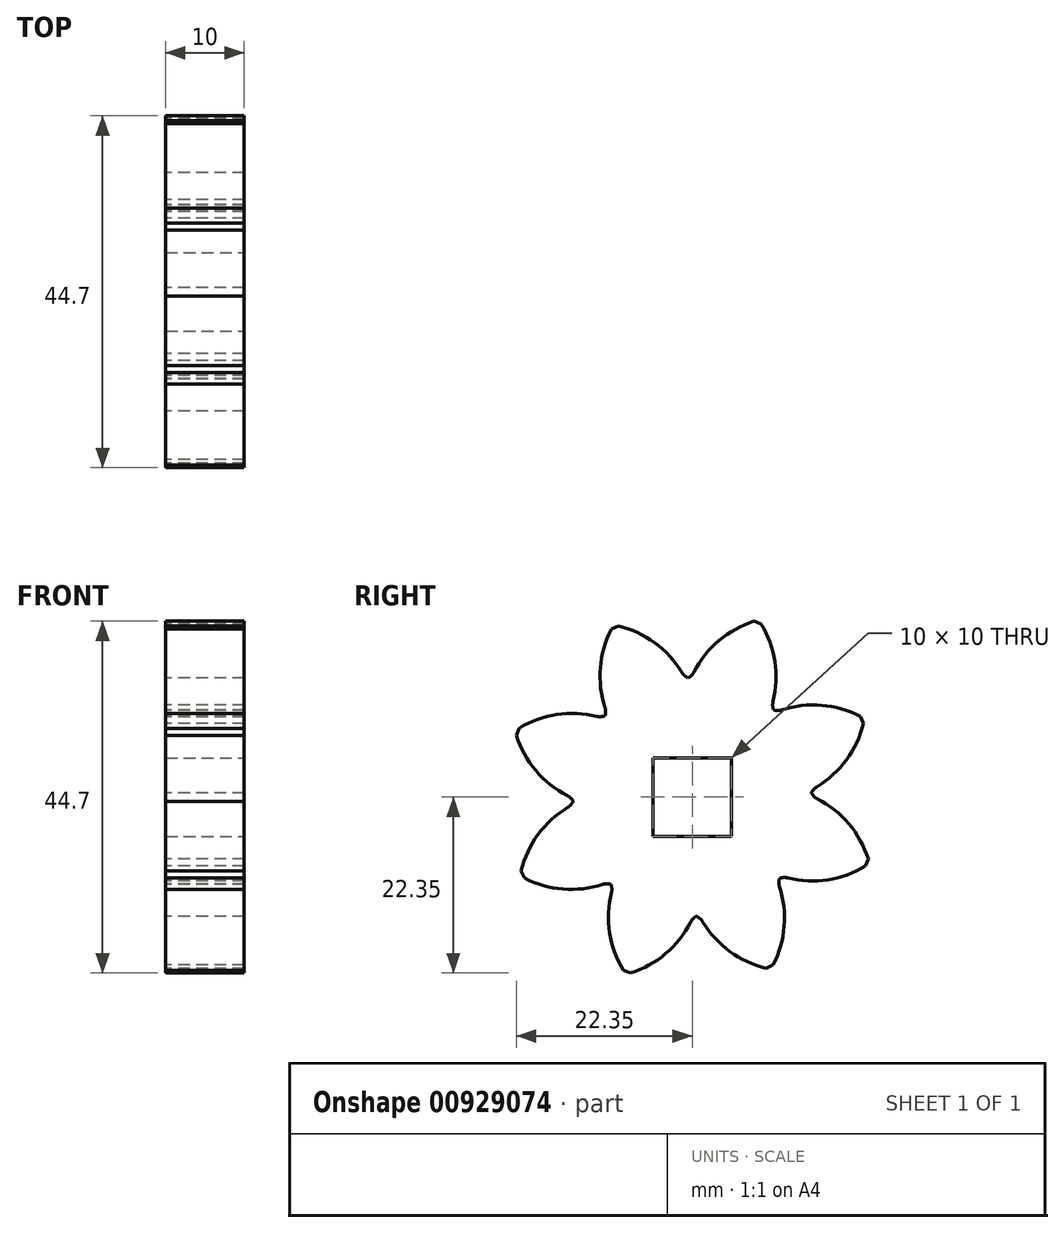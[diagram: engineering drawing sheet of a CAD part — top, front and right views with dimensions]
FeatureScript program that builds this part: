
annotation { "Feature Type Name" : "Feature", "Feature Type Description" : "" }
export const myFeature = defineFeature(function(context is Context, id is Id, definition is map)
    precondition{}
    {
        {
            var Q0;
            Q0=qCreatedBy(makeId("Right.planeOp"),FACE);
            var sketch = newSketch(context, id + "F0", { "sketchPlane" : qUnion([Q0])});
            skCircle(sketch, "E0", {"center": v(0, 0) * mm, "radius": 15 * mm, "construction": true});
            skCircle(sketch, "E1", {"center": v(0, 0) * mm, "radius": 25 * mm, "construction": true});
            skCircle(sketch, "E2", {"center": v(0, 0) * mm, "radius": 20 * mm, "construction": true});
            skLineSegment(sketch, "E3", {"start": v(0, 0) * mm, "end": v(12.29, 8.6) * mm, "construction": true});
            skLineSegment(sketch, "E4", {"start": v(0, 0) * mm, "end": v(5.13, 14.1) * mm, "construction": true});
            skLineSegment(sketch, "E5", {"start": v(0, 0) * mm, "end": v(14.1, 5.13) * mm, "construction": true});
            skLineSegment(sketch, "E6", {"start": v(14.1, 5.13) * mm, "end": v(7.83, 22.35) * mm, "construction": true});
            skLineSegment(sketch, "E7", {"start": v(5.13, 14.1) * mm, "end": v(0.21, 15.89) * mm, "construction": true});
            skLineSegment(sketch, "E8", {"start": v(12.29, 8.6) * mm, "end": v(4.03, 20.4) * mm, "construction": true});
            skArc(sketch, "E9", {"start": v(7.83, 22.35) * mm, "mid": v(3.37, 19.88) * mm, "end": v(0.21, 15.89) * mm});
            skArc(sketch, "E10", {"start": v(-1.19, 14.95) * mm, "mid": v(-0.37, 15.24) * mm, "end": v(0.21, 15.89) * mm});
            skLineSegment(sketch, "E11", {"start": v(0, 0) * mm, "end": v(10.92, 29.21) * mm, "construction": true});
            skPoint(sketch, "E12", {"position": v(3.21, 19.74) * mm});
            skLineSegment(sketch, "E13", {"start": v(0, 0) * mm, "end": v(3.21, 19.74) * mm, "construction": true});
            skArc(sketch, "E14.MirrorCS", {"start": v(8.75, 22) * mm, "mid": v(10.5, 17.22) * mm, "end": v(10.26, 12.13) * mm});
            skArc(sketch, "E15.MirrorCS", {"start": v(10.7, 10.5) * mm, "mid": v(10.27, 11.26) * mm, "end": v(10.26, 12.13) * mm});
            skLineSegment(sketch, "E16", {"start": v(8.75, 22) * mm, "end": v(7.83, 22.35) * mm});
            skArc(sketch, "E17.1.0", {"start": v(-10.27, 21.34) * mm, "mid": v(-11.67, 16.44) * mm, "end": v(-11.08, 11.38) * mm});
            skLineSegment(sketch, "E17.1.1", {"start": v(-9.37, 21.75) * mm, "end": v(-10.27, 21.34) * mm});
            skArc(sketch, "E17.1.2", {"start": v(0.14, 15) * mm, "mid": v(-0.7, 15.23) * mm, "end": v(-1.32, 15.83) * mm});
            skArc(sketch, "E17.1.3", {"start": v(-11.41, 9.73) * mm, "mid": v(-11.03, 10.51) * mm, "end": v(-11.08, 11.38) * mm});
            skArc(sketch, "E17.1.4", {"start": v(-9.37, 21.75) * mm, "mid": v(-4.75, 19.6) * mm, "end": v(-1.32, 15.83) * mm});
            skArc(sketch, "E17.2.0", {"start": v(-22.35, 7.83) * mm, "mid": v(-19.88, 3.37) * mm, "end": v(-15.89, 0.21) * mm});
            skLineSegment(sketch, "E17.2.1", {"start": v(-22, 8.75) * mm, "end": v(-22.35, 7.83) * mm});
            skArc(sketch, "E17.2.2", {"start": v(-10.5, 10.7) * mm, "mid": v(-11.26, 10.27) * mm, "end": v(-12.13, 10.26) * mm});
            skArc(sketch, "E17.2.3", {"start": v(-14.95, -1.19) * mm, "mid": v(-15.24, -0.37) * mm, "end": v(-15.89, 0.21) * mm});
            skArc(sketch, "E17.2.4", {"start": v(-22, 8.75) * mm, "mid": v(-17.22, 10.5) * mm, "end": v(-12.13, 10.26) * mm});
            skArc(sketch, "E17.3.0", {"start": v(-21.34, -10.27) * mm, "mid": v(-16.44, -11.67) * mm, "end": v(-11.38, -11.08) * mm});
            skLineSegment(sketch, "E17.3.1", {"start": v(-21.75, -9.37) * mm, "end": v(-21.34, -10.27) * mm});
            skArc(sketch, "E17.3.2", {"start": v(-15, 0.14) * mm, "mid": v(-15.23, -0.7) * mm, "end": v(-15.83, -1.32) * mm});
            skArc(sketch, "E17.3.3", {"start": v(-9.73, -11.41) * mm, "mid": v(-10.51, -11.03) * mm, "end": v(-11.38, -11.08) * mm});
            skArc(sketch, "E17.3.4", {"start": v(-21.75, -9.37) * mm, "mid": v(-19.6, -4.75) * mm, "end": v(-15.83, -1.32) * mm});
            skArc(sketch, "E17.4.0", {"start": v(-7.83, -22.35) * mm, "mid": v(-3.37, -19.88) * mm, "end": v(-0.21, -15.89) * mm});
            skLineSegment(sketch, "E17.4.1", {"start": v(-8.75, -22) * mm, "end": v(-7.83, -22.35) * mm});
            skArc(sketch, "E17.4.2", {"start": v(-10.7, -10.5) * mm, "mid": v(-10.27, -11.26) * mm, "end": v(-10.26, -12.13) * mm});
            skArc(sketch, "E17.4.3", {"start": v(1.19, -14.95) * mm, "mid": v(0.37, -15.24) * mm, "end": v(-0.21, -15.89) * mm});
            skArc(sketch, "E17.4.4", {"start": v(-8.75, -22) * mm, "mid": v(-10.5, -17.22) * mm, "end": v(-10.26, -12.13) * mm});
            skArc(sketch, "E17.5.0", {"start": v(10.27, -21.34) * mm, "mid": v(11.67, -16.44) * mm, "end": v(11.08, -11.38) * mm});
            skLineSegment(sketch, "E17.5.1", {"start": v(9.37, -21.75) * mm, "end": v(10.27, -21.34) * mm});
            skArc(sketch, "E17.5.2", {"start": v(-0.14, -15) * mm, "mid": v(0.7, -15.23) * mm, "end": v(1.32, -15.83) * mm});
            skArc(sketch, "E17.5.3", {"start": v(11.41, -9.73) * mm, "mid": v(11.03, -10.51) * mm, "end": v(11.08, -11.38) * mm});
            skArc(sketch, "E17.5.4", {"start": v(9.37, -21.75) * mm, "mid": v(4.75, -19.6) * mm, "end": v(1.32, -15.83) * mm});
            skArc(sketch, "E17.6.0", {"start": v(22.35, -7.83) * mm, "mid": v(19.88, -3.37) * mm, "end": v(15.89, -0.21) * mm});
            skLineSegment(sketch, "E17.6.1", {"start": v(22, -8.75) * mm, "end": v(22.35, -7.83) * mm});
            skArc(sketch, "E17.6.2", {"start": v(10.5, -10.7) * mm, "mid": v(11.26, -10.27) * mm, "end": v(12.13, -10.26) * mm});
            skArc(sketch, "E17.6.3", {"start": v(14.95, 1.19) * mm, "mid": v(15.24, 0.37) * mm, "end": v(15.89, -0.21) * mm});
            skArc(sketch, "E17.6.4", {"start": v(22, -8.75) * mm, "mid": v(17.22, -10.5) * mm, "end": v(12.13, -10.26) * mm});
            skArc(sketch, "E17.7.0", {"start": v(21.34, 10.27) * mm, "mid": v(16.44, 11.67) * mm, "end": v(11.38, 11.08) * mm});
            skLineSegment(sketch, "E17.7.1", {"start": v(21.75, 9.37) * mm, "end": v(21.34, 10.27) * mm});
            skArc(sketch, "E17.7.2", {"start": v(15, -0.14) * mm, "mid": v(15.23, 0.7) * mm, "end": v(15.83, 1.32) * mm});
            skArc(sketch, "E17.7.3", {"start": v(9.73, 11.41) * mm, "mid": v(10.51, 11.03) * mm, "end": v(11.38, 11.08) * mm});
            skArc(sketch, "E17.7.4", {"start": v(21.75, 9.37) * mm, "mid": v(19.6, 4.75) * mm, "end": v(15.83, 1.32) * mm});
            skSolve(sketch);
        }
        {
            var Q0;
            Q0 = qSketchRegion(id + "F0", true);
            extrude(context, id + "F1", {"entities" : qUnion([Q0]), "endBound" : BoundingType.SYMMETRIC, "depth" : 10 * mm, "offsetDistance" : 25 * mm});
        }
        {
            var Q0;
            Q0=qCreatedBy(makeId("Right.planeOp"),FACE);
            var sketch = newSketch(context, id + "F2", { "sketchPlane" : qUnion([Q0])});
            skLineSegment(sketch, "E18.bottom", {"start": v(-5, 5) * mm, "end": v(5, 5) * mm});
            skLineSegment(sketch, "E18.top", {"start": v(-5, -5) * mm, "end": v(5, -5) * mm});
            skLineSegment(sketch, "E18.left", {"start": v(-5, 5) * mm, "end": v(-5, -5) * mm});
            skLineSegment(sketch, "E18.right", {"start": v(5, 5) * mm, "end": v(5, -5) * mm});
            skSolve(sketch);
        }
        {
            var Q0;
            Q0 = qSketchRegion(id + "F2", true);
            extrude(context, id + "F3", {"entities" : qUnion([Q0]), "operationType" : NewBodyOperationType.REMOVE, "endBound" : BoundingType.THROUGH_ALL, "oppositeDirection" : true, "depth" : 25 * mm, "offsetDistance" : 25 * mm, "hasSecondDirection" : true, "secondDirectionBound" : SecondDirectionBoundingType.THROUGH_ALL, "secondDirectionOppositeDirection" : false, "secondDirectionDepth" : 25 * mm});
        }
    });
